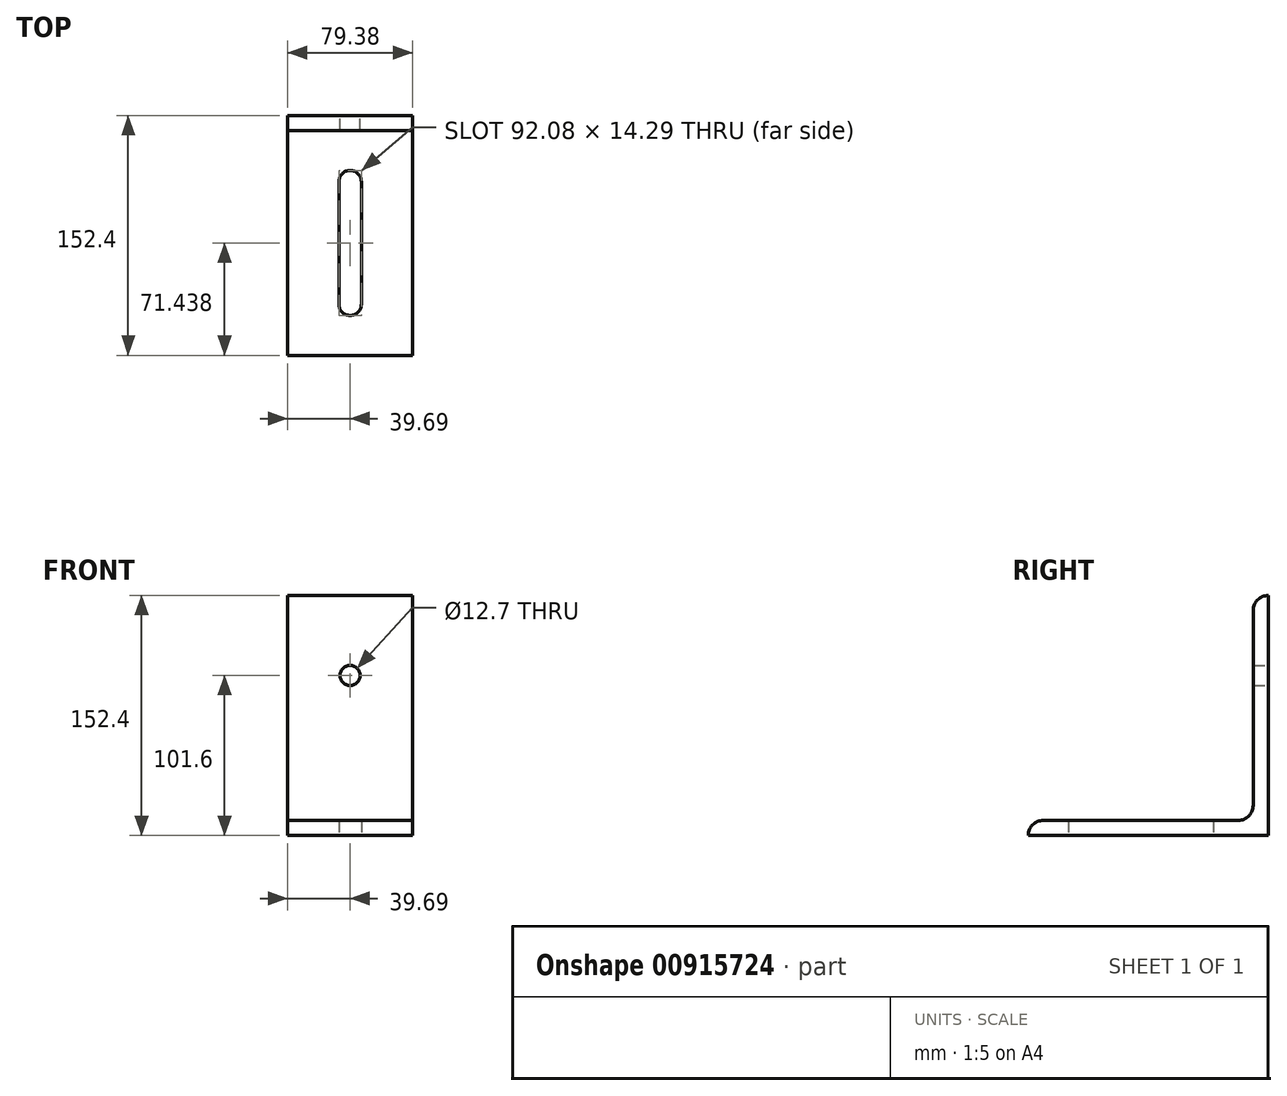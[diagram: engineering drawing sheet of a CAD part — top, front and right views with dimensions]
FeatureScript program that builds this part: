
annotation { "Feature Type Name" : "Feature", "Feature Type Description" : "" }
export const myFeature = defineFeature(function(context is Context, id is Id, definition is map)
    precondition{}
    {
        {
            var Q0;
            Q0=qCreatedBy(makeId("Right.planeOp"),FACE);
            var sketch = newSketch(context, id + "F0", { "sketchPlane" : qUnion([Q0])});
            skLineSegment(sketch, "E0", {"start": v(0, 152.4) * mm, "end": v(0, 0) * mm});
            skLineSegment(sketch, "E1", {"start": v(0, 0) * mm, "end": v(-152.4, 0) * mm});
            skLineSegment(sketch, "E2", {"start": v(-152.4, 0) * mm, "end": v(-152.4, 0) * mm});
            skLineSegment(sketch, "E3", {"start": v(-142.88, 9.52) * mm, "end": v(-19.05, 9.53) * mm});
            skLineSegment(sketch, "E4", {"start": v(-9.52, 19.05) * mm, "end": v(-9.52, 142.88) * mm});
            skLineSegment(sketch, "E5", {"start": v(0, 152.4) * mm, "end": v(0, 152.4) * mm});
            skPoint(sketch, "E6.visualSharp", {"position": v(-9.52, 152.4) * mm});
            skArc(sketch, "E6.filletArc", {"start": v(0, 152.4) * mm, "mid": v(-6.74, 149.61) * mm, "end": v(-9.53, 142.88) * mm});
            skPoint(sketch, "E7.visualSharp", {"position": v(-152.4, 9.52) * mm});
            skArc(sketch, "E7.filletArc", {"start": v(-142.88, 9.52) * mm, "mid": v(-149.61, 6.74) * mm, "end": v(-152.4, 0) * mm});
            skPoint(sketch, "E8.visualSharp", {"position": v(-9.53, 9.53) * mm});
            skArc(sketch, "E8.filletArc", {"start": v(-19.05, 9.53) * mm, "mid": v(-12.31, 12.31) * mm, "end": v(-9.52, 19.05) * mm});
            skSolve(sketch);
        }
        {
            var Q0;
            Q0=qSketchRegion(id+"F0",true);
            extrude(context, id + "F1", {"entities" : qUnion([Q0]), "depth" : 79.38 * mm, "offsetDistance" : 25.4 * mm, "symmetric" : true});
        }
        {
            var Q0;
            Q0=makeQuery(id+"F1.opExtrude","SWEPT_FACE",FACE,{"disambiguationData":[OSD([sQuery(id+"F0.wireOp",EDGE,"E0")])]});
            var sketch = newSketch(context, id + "F2", { "sketchPlane" : qUnion([Q0])});
            skCircle(sketch, "E9", {"center": v(0, 101.6) * mm, "radius": 6.35 * mm});
            skSolve(sketch);
        }
        {
            var Q0;
            Q0=qSketchRegion(id+"F2",true);
            extrude(context, id + "F3", {"entities" : qUnion([Q0]), "operationType" : NewBodyOperationType.REMOVE, "oppositeDirection" : true, "depth" : 25.4 * mm, "offsetDistance" : 25.4 * mm});
        }
        {
            var Q0;
            Q0=makeQuery(id+"F1.opExtrude","SWEPT_FACE",FACE,{"disambiguationData":[OSD([sQuery(id+"F0.wireOp",EDGE,"E1")])]});
            var sketch = newSketch(context, id + "F4", { "sketchPlane" : qUnion([Q0])});
            skLineSegment(sketch, "E10.bottom", {"start": v(7.14, 119.86) * mm, "end": v(-7.14, 119.86) * mm});
            skLineSegment(sketch, "E10.top", {"start": v(7.14, 42.07) * mm, "end": v(-7.14, 42.07) * mm});
            skLineSegment(sketch, "E10.left", {"start": v(7.14, 119.86) * mm, "end": v(7.14, 42.07) * mm});
            skLineSegment(sketch, "E10.right", {"start": v(-7.14, 119.86) * mm, "end": v(-7.14, 42.07) * mm});
            skPoint(sketch, "E10.middle", {"position": v(0, 80.96) * mm});
            skArc(sketch, "E11", {"start": v(-7.14, 42.07) * mm, "mid": v(0, 34.92) * mm, "end": v(7.14, 42.07) * mm});
            skArc(sketch, "E12", {"start": v(7.14, 119.86) * mm, "mid": v(0, 127) * mm, "end": v(-7.14, 119.86) * mm});
            skPoint(sketch, "E13", {"position": v(0, 152.4) * mm});
            skPoint(sketch, "E14", {"position": v(0, 127) * mm});
            skPoint(sketch, "E15", {"position": v(0, 34.92) * mm});
            skSolve(sketch);
        }
        {
            var Q0;
            Q0=qSketchRegion(id+"F4",true);
            extrude(context, id + "F5", {"entities" : qUnion([Q0]), "operationType" : NewBodyOperationType.REMOVE, "oppositeDirection" : true, "depth" : 25.4 * mm, "offsetDistance" : 25.4 * mm});
        }
    });
